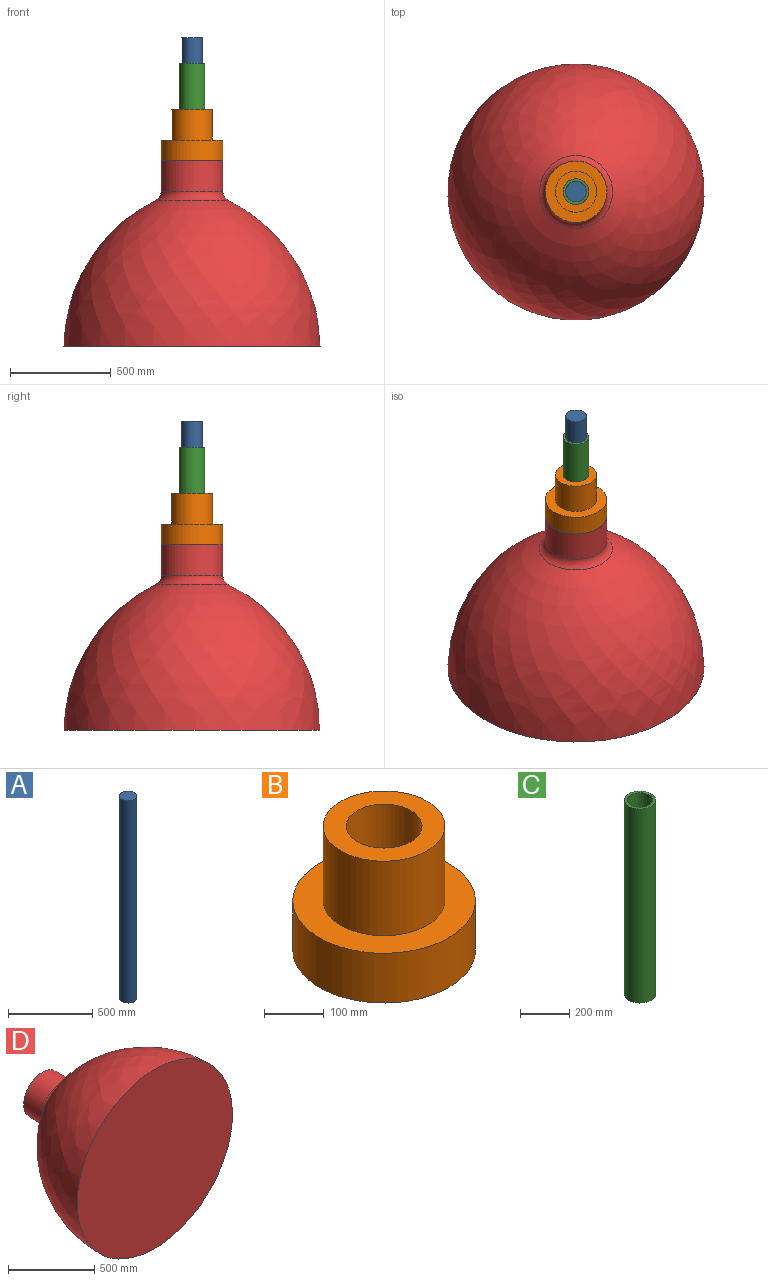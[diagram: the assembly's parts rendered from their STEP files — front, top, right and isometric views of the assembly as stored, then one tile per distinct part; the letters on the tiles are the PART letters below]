
ASSEMBLY  parts=4 mates=3
PART A: 3 faces, bbox 101.6x101.6x1473.2 mm
  f0: cylinder r=50.8mm len=1473.2mm, axis (0,0,-1), area 470224.5mm2, adj f1,f2
  f1: plane 101.6x101.6mm, normal (0,0,1), area 8107.3mm2, adj f0
  f2: plane 101.6x101.6mm, normal (0,0,-1), area 8107.3mm2, adj f0
PART B: 6 faces, bbox 304.8x304.8x254 mm
  f0: cylinder r=152.4mm len=304.8mm, axis (0,0,-1), area 97287.8mm2, adj f1,f2
  f1: plane 304.8x304.8mm, normal (0,0,1), area 40536.6mm2, adj f0,f3
  f2: plane 304.8x304.8mm, normal (0,0,-1), area 60298.2mm2, adj f0,f5
  f3: cylinder r=101.6mm len=203.2mm, axis (0,0,-1), area 97287.8mm2, adj f1,f4
  f4: plane 203.2x203.2mm, normal (0,0,1), area 19761.6mm2, adj f3,f5
  f5: cylinder r=63.5mm len=254mm, axis (0,0,1), area 101341.5mm2, adj f2,f4
PART C: 4 faces, bbox 127x127x965.2 mm
  f0: cylinder r=63.5mm len=965.2mm, axis (0,0,1), area 385097.7mm2, adj f1,f2
  f1: plane 127x127mm, normal (0,0,-1), area 4560.4mm2, adj f0,f3
  f2: plane 127x127mm, normal (0,0,1), area 4560.4mm2, adj f0,f3
  f3: cylinder r=50.8mm len=965.2mm, axis (0,0,1), area 308078.1mm2, adj f1,f2
PART D: 10 faces, bbox 1270x921.3x1270 mm
  f0: revolved ~1270x1270mm, area 2689469.3mm2, adj f1,f2
  f1: plane 1270x1270mm, normal (0,-1,0), area 1266768.7mm2, adj f0
  f2: torus R=203.2mm, axis (0,-1,0), area 57695.5mm2, adj f0,f4
  f3: plane 279.4x279.4mm, normal (0,-1,0), area 43070.1mm2, adj f5,f9
  f4: cylinder r=152.4mm len=304.8mm, axis (0,-1,0), area 145931.8mm2, adj f2,f6
  f5: cylinder r=76.2mm len=152.4mm, axis (0,-1,0), area 72965.9mm2, adj f3,f6
  f6: plane 304.8x304.8mm, normal (0,1,0), area 54724.4mm2, adj f4,f5
  f7: plane 1244.2x1244.2mm, normal (0,1,0), area 1215829.5mm2, adj f8
  f8: revolved ~1244.2x1244.2mm, area 2540599mm2, adj f7,f9
  f9: torus R=203.2mm, axis (0,-1,0), area 67572mm2, adj f3,f8
PLACE A t=(-1645.19,3198.99,-2056.8)mm
PLACE B t=(-1348.36,3198.99,-1193.2)mm
PLACE C t=(-1832.76,3198.99,-710.6)mm
PLACE D rot(axis=(1,0,0),90deg) t=(-21414.95,1827.39,-5060.91)mm
MATE fastened A.f0 <-> B.f0  axis (0,0,-1) through (6195.44,1827.39,-1320.2)mm
MATE fastened B.f0 <-> D.f2  axis (0,0,1) through (6195.44,1827.39,-1193.2)mm
MATE fastened C.f0 <-> B.f0  axis (0,0,1) through (6195.44,1827.39,-1193.2)mm
